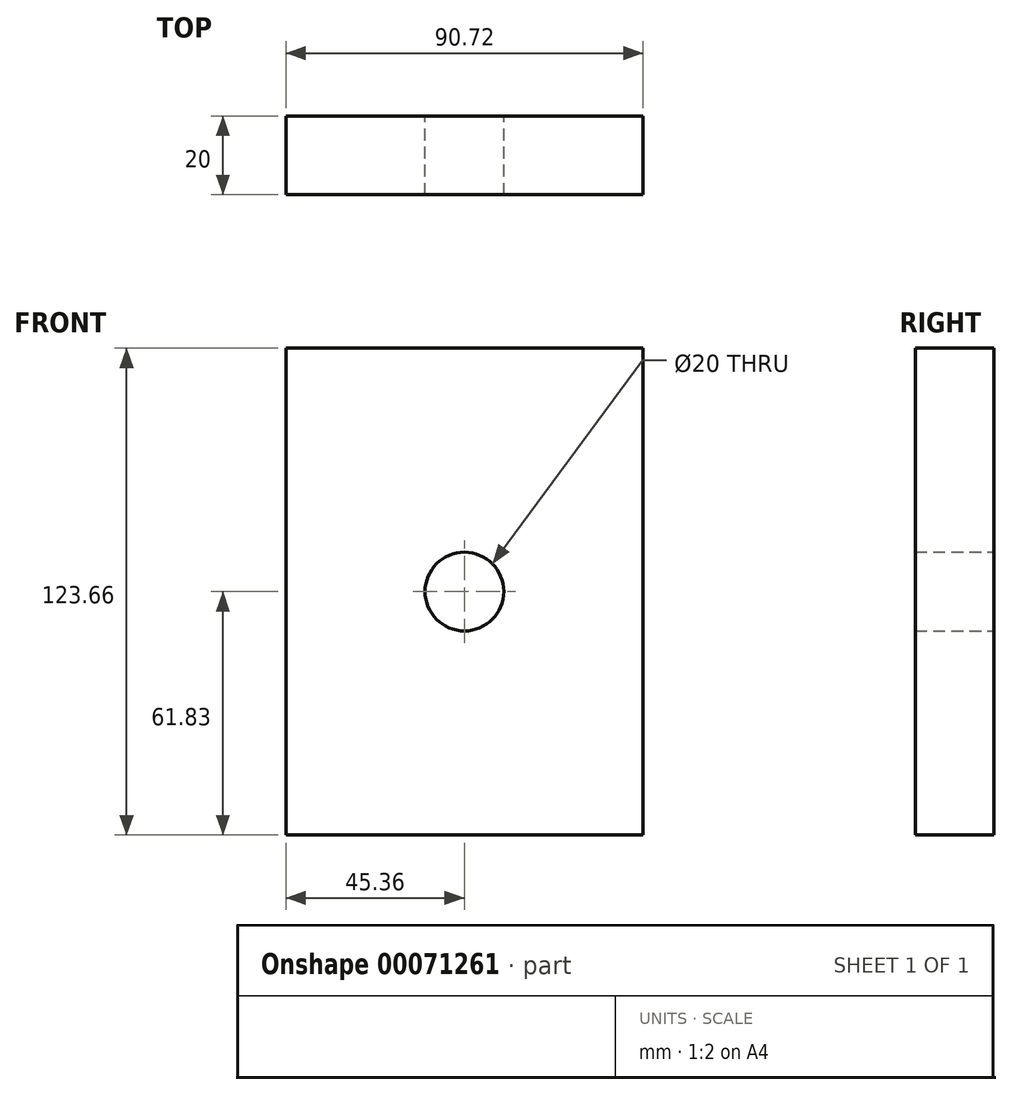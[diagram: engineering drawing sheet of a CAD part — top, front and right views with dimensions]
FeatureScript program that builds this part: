
annotation { "Feature Type Name" : "Feature", "Feature Type Description" : "" }
export const myFeature = defineFeature(function(context is Context, id is Id, definition is map)
    precondition{}
    {
        {
            var Q0;
            Q0=qCreatedBy(makeId("Front.planeOp"),FACE);
            var sketch = newSketch(context, id + "F0", { "sketchPlane" : qUnion([Q0])});
            skLineSegment(sketch, "E0.rect.bottom", {"start": v(-45.36, 61.83) * mm, "end": v(45.36, 61.83) * mm});
            skLineSegment(sketch, "E0.rect.top", {"start": v(-45.36, -61.83) * mm, "end": v(45.36, -61.83) * mm});
            skLineSegment(sketch, "E0.rect.left", {"start": v(-45.36, 61.83) * mm, "end": v(-45.36, -61.83) * mm});
            skLineSegment(sketch, "E0.rect.right", {"start": v(45.36, 61.83) * mm, "end": v(45.36, -61.83) * mm});
            skPoint(sketch, "E0.rect.middle", {"position": v(0, 0) * mm});
            skSolve(sketch);
        }
        {
            var Q0;
            Q0=makeQuery(id+"F0.imprint","IMPRINT",FACE,{"disambiguationData":[TD([[makeQuery(id+"F0.imprint","IMPRINT",EDGE,{"derivedFrom":sQuery(id+"F0.wireOp",EDGE,"E0.rect.bottom")}),-1.0]])]});
            extrude(context, id + "F1", {"entities" : qUnion([Q0]), "depth" : 20 * mm});
        }
        {
            var Q0;
            Q0=makeQuery(id+"F1.opExtrude","CAP_FACE",FACE,{"disambiguationData":[OSD([sQuery(id+"F0.wireOp",EDGE,"E0.rect.bottom"),sQuery(id+"F0.wireOp",EDGE,"E0.rect.top"),sQuery(id+"F0.wireOp",EDGE,"E0.rect.left"),sQuery(id+"F0.wireOp",EDGE,"E0.rect.right")])],"isStart":true});
            var sketch = newSketch(context, id + "F2", { "sketchPlane" : qUnion([Q0])});
            skCircle(sketch, "E1", {"center": v(0, 0) * mm, "radius": 10 * mm});
            skSolve(sketch);
        }
        {
            var Q0;
            Q0 = qSketchRegion(id + "F2", true);
            extrude(context, id + "F3", {"entities" : qUnion([Q0]), "operationType" : NewBodyOperationType.REMOVE, "oppositeDirection" : true, "depth" : 25 * mm});
        }
    });
